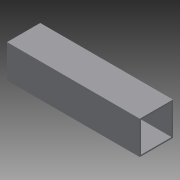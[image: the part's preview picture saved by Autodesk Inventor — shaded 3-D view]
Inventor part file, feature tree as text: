
AUTODESK INVENTOR PART (.ipt)
format: ipt  version: 2015 (Build 190159000, 159)  size: 74,752 bytes
history: native  units: in
note: dims shown in document units (in); Inventor stores cm internally (conversion verified against a paired STEP export)
features: extrude x1, sketch x1
ambient origin geometry x8: Origin, YZ Plane, XZ Plane, XY Plane, X Axis, Y Axis, Z Axis, Center Point
bodies: Solid1 (feature_tree)
feature tree (2):
  extrude  "Extrusion1"  Depth=2.0in
  sketch  "Sketch1"  dims[d0=2.0in d1=2.0in d2=0.083in d3=8.0in d4=0.0in]
